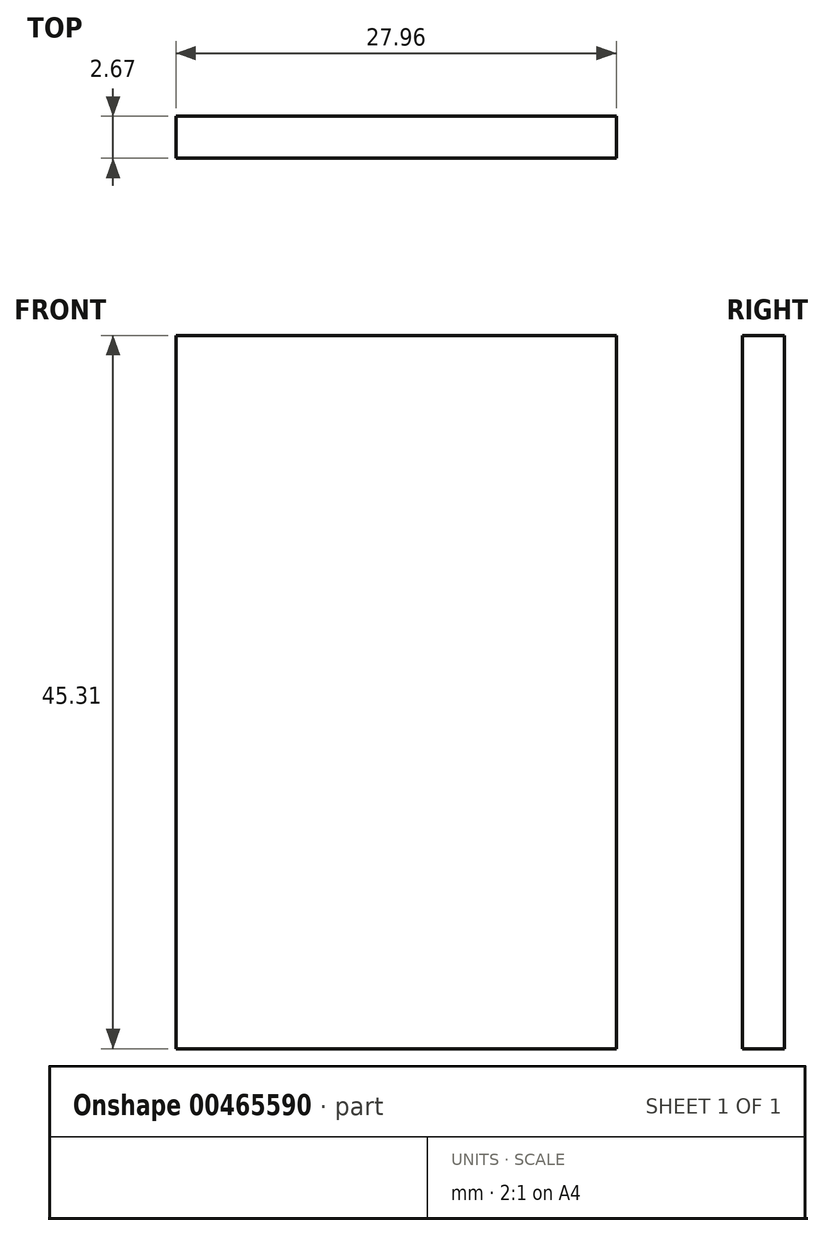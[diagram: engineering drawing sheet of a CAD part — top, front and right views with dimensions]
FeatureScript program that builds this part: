
annotation { "Feature Type Name" : "Feature", "Feature Type Description" : "" }
export const myFeature = defineFeature(function(context is Context, id is Id, definition is map)
    precondition{}
    {
        {
            var Q0;
            Q0=qCreatedBy(makeId("Front.planeOp"),FACE);
            var sketch = newSketch(context, id + "F0", { "sketchPlane" : qUnion([Q0])});
            skLineSegment(sketch, "E0.bottom", {"start": v(27.96, 0) * mm, "end": v(0, 0) * mm});
            skLineSegment(sketch, "E0.top", {"start": v(27.96, 45.3) * mm, "end": v(0, 45.3) * mm});
            skLineSegment(sketch, "E0.left", {"start": v(27.96, 0) * mm, "end": v(27.96, 45.3) * mm});
            skLineSegment(sketch, "E0.right", {"start": v(0, 0) * mm, "end": v(0, 45.3) * mm});
            skSolve(sketch);
        }
        {
            var Q0;
            Q0 = qSketchRegion(id + "F0", true);
            extrude(context, id + "F1", {"entities" : qUnion([Q0]), "depth" : 2.67 * mm});
        }
    });
